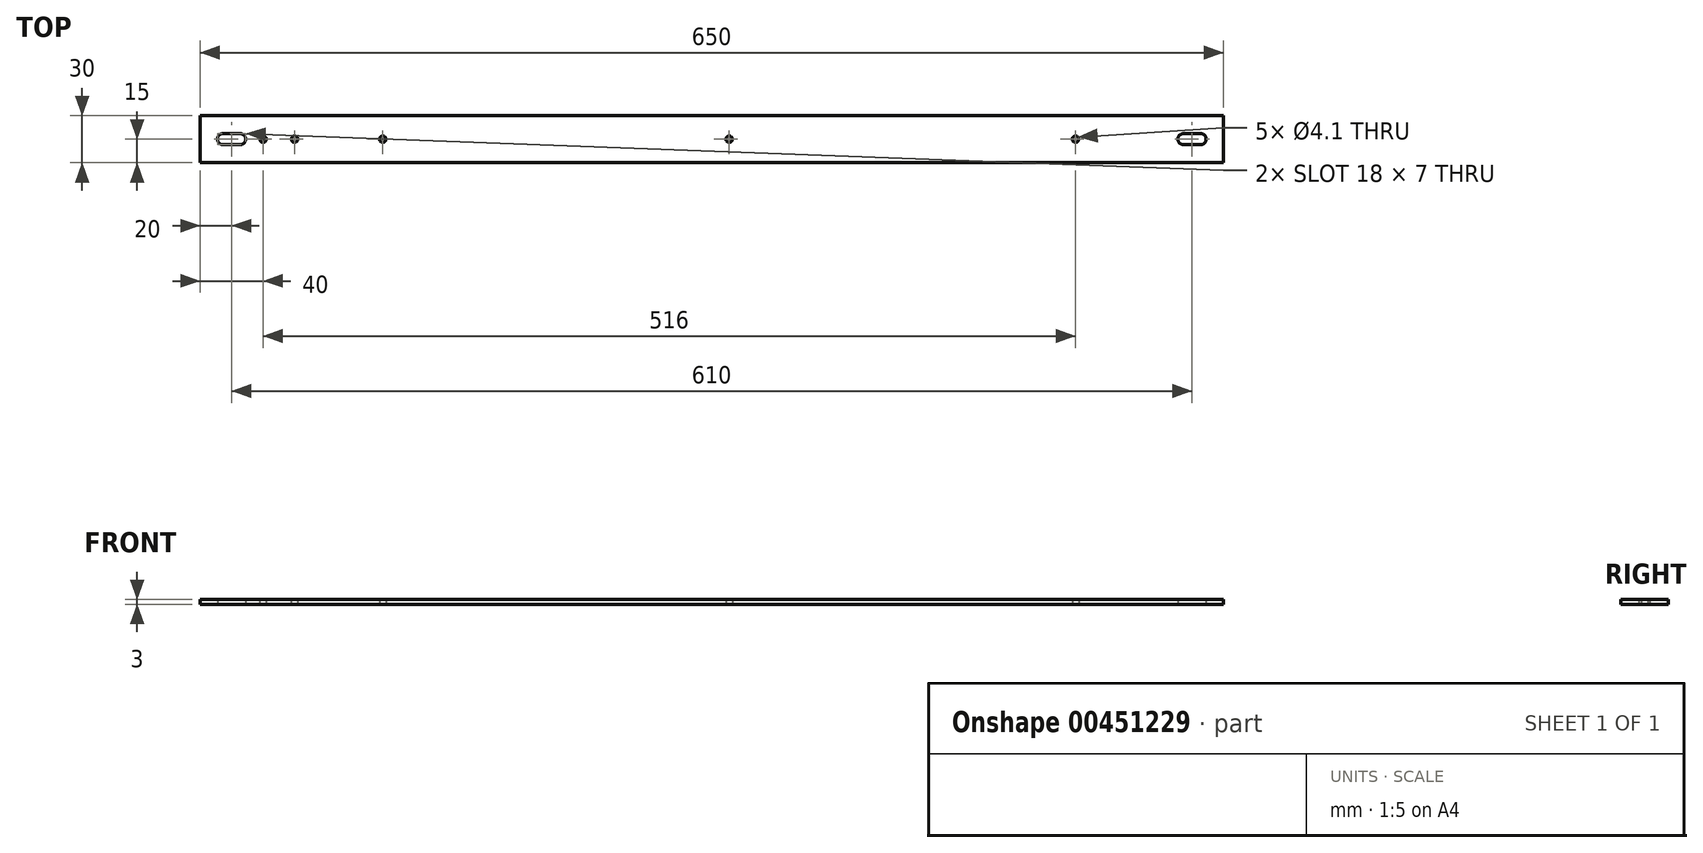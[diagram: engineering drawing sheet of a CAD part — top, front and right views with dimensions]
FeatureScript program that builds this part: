
annotation { "Feature Type Name" : "Feature", "Feature Type Description" : "" }
export const myFeature = defineFeature(function(context is Context, id is Id, definition is map)
    precondition{}
    {
        {
            var Q0;
            Q0=qCreatedBy(makeId("Top.planeOp"),FACE);
            var sketch = newSketch(context, id + "F0", { "sketchPlane" : qUnion([Q0])});
            skLineSegment(sketch, "E0.bottom", {"start": v(250, -15) * mm, "end": v(-250, -15) * mm});
            skLineSegment(sketch, "E0.top", {"start": v(250, 15) * mm, "end": v(-250, 15) * mm});
            skLineSegment(sketch, "E0.left", {"start": v(250, -15) * mm, "end": v(250, 15) * mm});
            skLineSegment(sketch, "E0.right", {"start": v(-250, -15) * mm, "end": v(-250, 15) * mm});
            skPoint(sketch, "E0.middle", {"position": v(0, 0) * mm});
            skLineSegment(sketch, "E1.bottom", {"start": v(-224.5, -3.5) * mm, "end": v(-235.5, -3.5) * mm});
            skLineSegment(sketch, "E1.top", {"start": v(-224.5, 3.5) * mm, "end": v(-235.5, 3.5) * mm});
            skLineSegment(sketch, "E1.left", {"start": v(-224.5, -3.5) * mm, "end": v(-224.5, 3.5) * mm, "construction": true});
            skLineSegment(sketch, "E1.right", {"start": v(-235.5, -3.5) * mm, "end": v(-235.5, 3.5) * mm, "construction": true});
            skPoint(sketch, "E1.middle", {"position": v(-230, 0) * mm});
            skArc(sketch, "E2", {"start": v(-235.5, 3.5) * mm, "mid": v(-239, 0) * mm, "end": v(-235.5, -3.5) * mm});
            skArc(sketch, "E3", {"start": v(-224.5, -3.5) * mm, "mid": v(-221, 0) * mm, "end": v(-224.5, 3.5) * mm});
            skCircle(sketch, "E4", {"center": v(-210, 0) * mm, "radius": 2.05 * mm});
            skCircle(sketch, "E5", {"center": v(-190, 0) * mm, "radius": 2.05 * mm});
            skCircle(sketch, "E6", {"center": v(-134, 0) * mm, "radius": 2.05 * mm});
            skCircle(sketch, "E7", {"center": v(306, 0) * mm, "radius": 2.05 * mm});
            skLineSegment(sketch, "E8", {"start": v(250, 15) * mm, "end": v(400, 15) * mm});
            skLineSegment(sketch, "E9", {"start": v(400, 15) * mm, "end": v(400, -15) * mm});
            skLineSegment(sketch, "E10", {"start": v(400, -15) * mm, "end": v(250, -15) * mm});
            skLineSegment(sketch, "E11.bottom", {"start": v(385.5, -3.5) * mm, "end": v(374.5, -3.5) * mm});
            skLineSegment(sketch, "E11.top", {"start": v(385.5, 3.5) * mm, "end": v(374.5, 3.5) * mm});
            skLineSegment(sketch, "E11.left", {"start": v(385.5, -3.5) * mm, "end": v(385.5, 3.5) * mm, "construction": true});
            skLineSegment(sketch, "E11.right", {"start": v(374.5, -3.5) * mm, "end": v(374.5, 3.5) * mm, "construction": true});
            skPoint(sketch, "E11.middle", {"position": v(380, 0) * mm});
            skArc(sketch, "E12", {"start": v(374.5, 3.5) * mm, "mid": v(371, 0) * mm, "end": v(374.5, -3.5) * mm});
            skArc(sketch, "E13", {"start": v(385.5, -3.5) * mm, "mid": v(389, 0) * mm, "end": v(385.5, 3.5) * mm});
            skPoint(sketch, "E14", {"position": v(400, 0) * mm});
            skCircle(sketch, "E15", {"center": v(86, 0) * mm, "radius": 2.05 * mm});
            skSolve(sketch);
        }
        {
            var Q0;
            Q0 = qSketchRegion(id + "F0", true);
            extrude(context, id + "F1", {"entities" : qUnion([Q0]), "depth" : 3 * mm, "offsetDistance" : 25 * mm});
        }
    });
